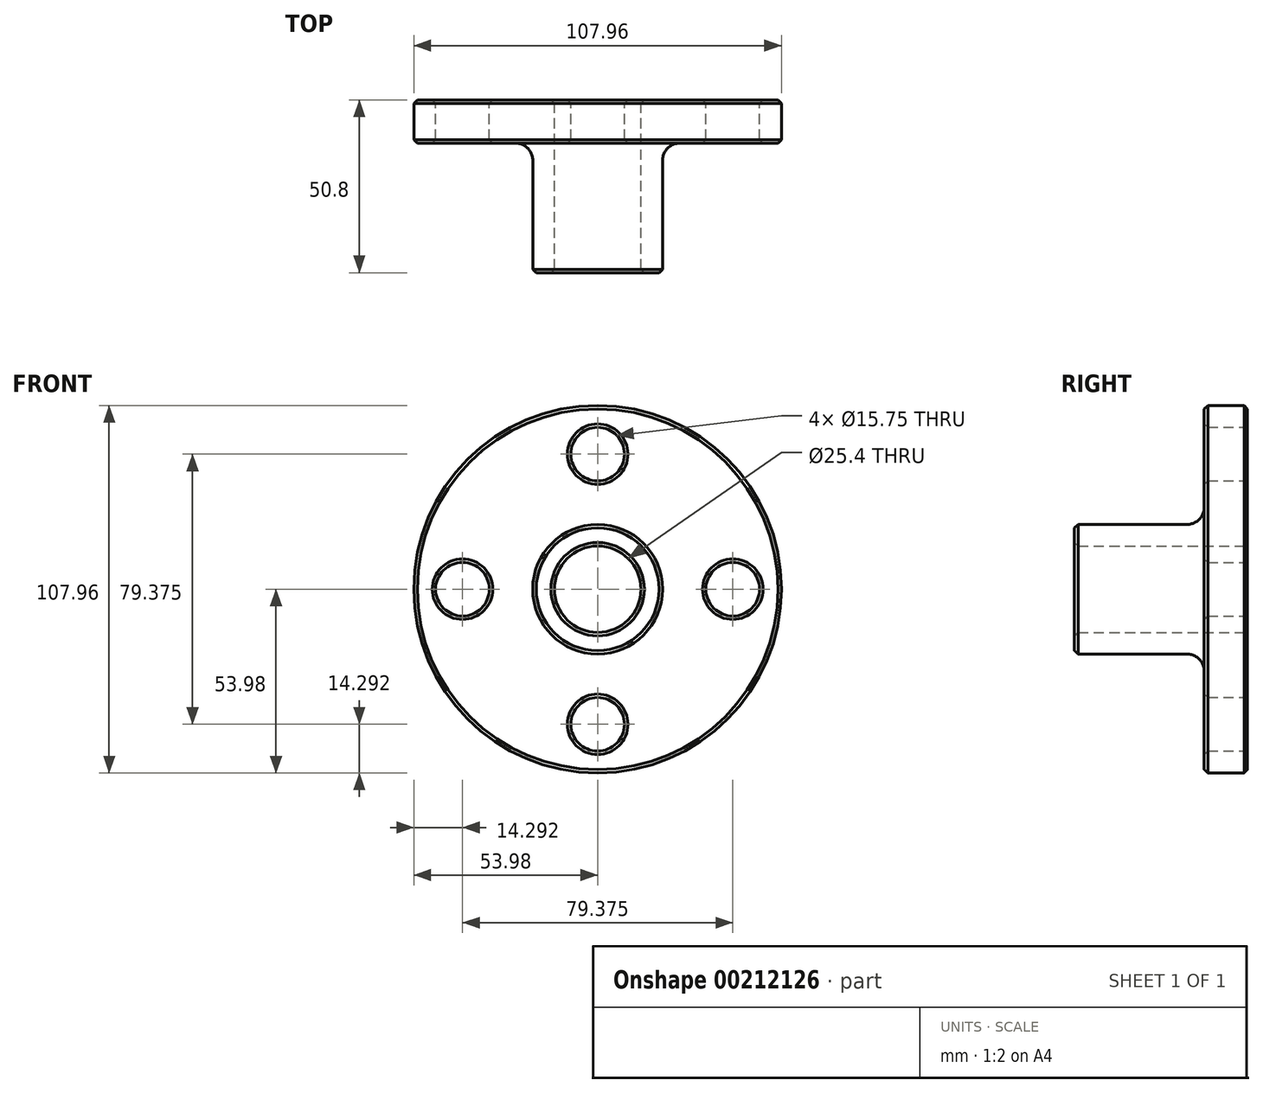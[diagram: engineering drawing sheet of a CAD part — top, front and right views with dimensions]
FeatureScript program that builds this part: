
annotation { "Feature Type Name" : "Feature", "Feature Type Description" : "" }
export const myFeature = defineFeature(function(context is Context, id is Id, definition is map)
    precondition{}
    {
        {
            var Q0;
            Q0=qCreatedBy(makeId("Front.planeOp"),FACE);
            var sketch = newSketch(context, id + "F0", { "sketchPlane" : qUnion([Q0])});
            skCircle(sketch, "E0", {"center": v(0, 0) * mm, "radius": 12.7 * mm});
            skCircle(sketch, "E1", {"center": v(0, 0) * mm, "radius": 39.69 * mm});
            skCircle(sketch, "E2", {"center": v(0, 0) * mm, "radius": 53.98 * mm});
            skCircle(sketch, "E3", {"center": v(-39.69, 0) * mm, "radius": 7.87 * mm});
            skCircle(sketch, "E4.1.0", {"center": v(0, -39.69) * mm, "radius": 7.87 * mm});
            skCircle(sketch, "E4.2.0", {"center": v(39.69, 0) * mm, "radius": 7.87 * mm});
            skCircle(sketch, "E4.3.0", {"center": v(0, 39.69) * mm, "radius": 7.87 * mm});
            skCircle(sketch, "E5", {"center": v(0, 0) * mm, "radius": 19.05 * mm});
            skSolve(sketch);
        }
        {
            var Q0;
            Q0=makeQuery(id+"F0.imprint","IMPRINT",FACE,{"disambiguationData":[TD([[makeQuery(id+"F0.imprint","IMPRINT",EDGE,{"derivedFrom":sQuery(id+"F0.wireOp",EDGE,"E2")}),1.0]])]});
            var Q1;
            Q1=makeQuery(id+"F0.imprint","IMPRINT",FACE,{"disambiguationData":[TD([[makeQuery(id+"F0.imprint","IMPRINT",EDGE,{"derivedFrom":sQuery(id+"F0.wireOp",EDGE,"E5")}),-1.0]])]});
            var Q2;
            Q2=makeQuery(id+"F0.imprint","IMPRINT",FACE,{"disambiguationData":[TD([[makeQuery(id+"F0.imprint","IMPRINT",EDGE,{"derivedFrom":sQuery(id+"F0.wireOp",EDGE,"E0")}),-1.0]])]});
            extrude(context, id + "F1", {"entities" : qUnion([Q0, Q1, Q2]), "depth" : 12.7 * mm});
        }
        {
            var Q0;
            Q0=makeQuery(id+"F0.imprint","IMPRINT",FACE,{"disambiguationData":[TD([[makeQuery(id+"F0.imprint","IMPRINT",EDGE,{"derivedFrom":sQuery(id+"F0.wireOp",EDGE,"E0")}),-1.0]])]});
            extrude(context, id + "F2", {"entities" : qUnion([Q0]), "operationType" : NewBodyOperationType.ADD, "depth" : 50.8 * mm});
        }
        {
            var Q0;
            Q0=makeQuery(id+"F2.boolean.opBoolean","INTERSECT",EDGE,{"derivedFrom":[makeQuery(id+"F1.opExtrude","CAP_FACE",FACE,{"disambiguationData":[OSD([sQuery(id+"F0.wireOp",EDGE,"E0"),sQuery(id+"F0.wireOp",EDGE,"E2"),sQuery(id+"F0.wireOp",EDGE,"E3"),sQuery(id+"F0.wireOp",EDGE,"E4.1.0"),sQuery(id+"F0.wireOp",EDGE,"E4.2.0"),sQuery(id+"F0.wireOp",EDGE,"E4.3.0")])],"isStart":false}),makeQuery(id+"F2.opExtrude","SWEPT_FACE",FACE,{"disambiguationData":[OSD([sQuery(id+"F0.wireOp",EDGE,"E5")])]})]});
            fillet(context, id + "F3", {"entities" : qUnion([Q0]), "radius" : 5.08 * mm, "tangentPropagation" : true, "allowEdgeOverflow" : false});
        }
        {
            var Q0;
            Q0=makeQuery(id+"F1.opExtrude","SWEPT_FACE",FACE,{"disambiguationData":[OSD([sQuery(id+"F0.wireOp",EDGE,"E2")])]});
            var Q1;
            Q1=makeQuery(id+"F1.opExtrude","SWEPT_FACE",FACE,{"disambiguationData":[OSD([sQuery(id+"F0.wireOp",EDGE,"E3")])]});
            var Q2;
            Q2=makeQuery(id+"F1.opExtrude","SWEPT_FACE",FACE,{"disambiguationData":[OSD([sQuery(id+"F0.wireOp",EDGE,"E4.1.0")])]});
            var Q3;
            Q3=makeQuery(id+"F1.opExtrude","SWEPT_FACE",FACE,{"disambiguationData":[OSD([sQuery(id+"F0.wireOp",EDGE,"E4.2.0")])]});
            var Q4;
            Q4=makeQuery(id+"F1.opExtrude","SWEPT_FACE",FACE,{"disambiguationData":[OSD([sQuery(id+"F0.wireOp",EDGE,"E4.3.0")])]});
            var Q5;
            Q5=makeQuery(id+"F2.opExtrude","CAP_EDGE",EDGE,{"disambiguationData":[OSD([sQuery(id+"F0.wireOp",EDGE,"E5")])],"isStart":false});
            var Q6;
            {var subQ0=sQuery(id+"F0.wireOp",EDGE,"E0");Q6=makeQuery(id+"F2.boolean.opBoolean","MERGE",FACE,{"derivedFrom":[makeQuery(id+"F1.opExtrude","SWEPT_FACE",FACE,{"disambiguationData":[OSD([subQ0])]}),makeQuery(id+"F2.opExtrude","SWEPT_FACE",FACE,{"disambiguationData":[OSD([subQ0])]})]});}
            chamfer(context, id + "F4", {"entities" : qUnion([Q0, Q1, Q2, Q3, Q4, Q5, Q6]), "width" : 1.02 * mm, "tangentPropagation" : true});
        }
    });
